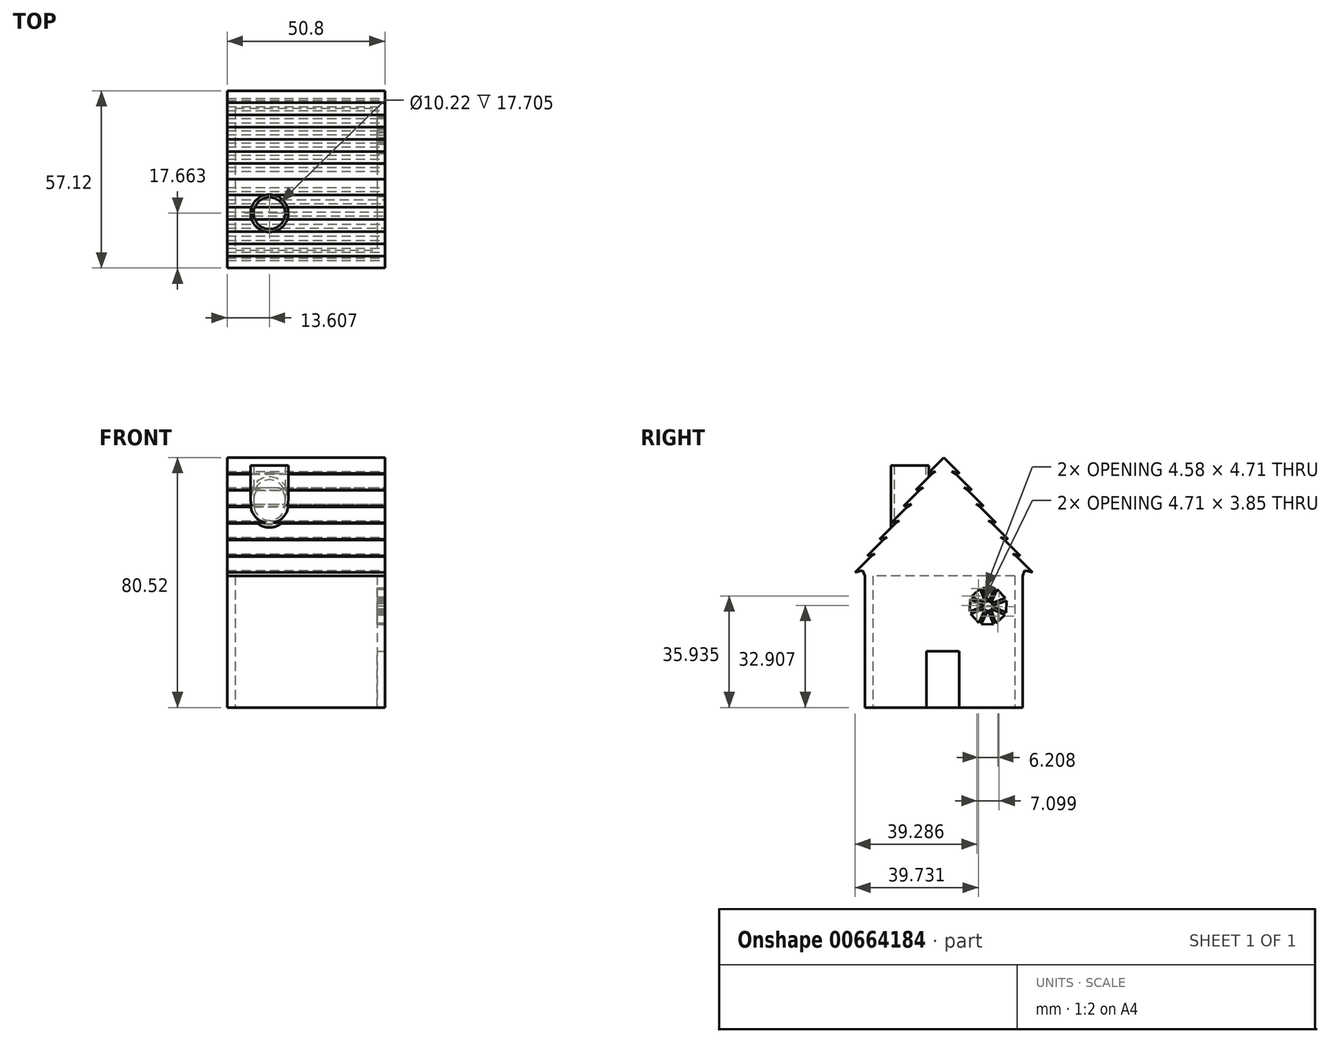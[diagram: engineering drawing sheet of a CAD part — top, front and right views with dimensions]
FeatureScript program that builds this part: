
annotation { "Feature Type Name" : "Feature", "Feature Type Description" : "" }
export const myFeature = defineFeature(function(context is Context, id is Id, definition is map)
    precondition{}
    {
        {
            var Q0;
            Q0=qCreatedBy(makeId("Top.planeOp"),FACE);
            var sketch = newSketch(context, id + "F0", { "sketchPlane" : qUnion([Q0])});
            skLineSegment(sketch, "E0.bottom", {"start": v(-25.4, 25.4) * mm, "end": v(25.4, 25.4) * mm});
            skLineSegment(sketch, "E0.top", {"start": v(-25.4, -25.4) * mm, "end": v(25.4, -25.4) * mm});
            skLineSegment(sketch, "E0.left", {"start": v(-25.4, 25.4) * mm, "end": v(-25.4, -25.4) * mm});
            skLineSegment(sketch, "E0.right", {"start": v(25.4, 25.4) * mm, "end": v(25.4, -25.4) * mm});
            skLineSegment(sketch, "E1.bottom", {"start": v(-22.86, 22.86) * mm, "end": v(22.86, 22.86) * mm});
            skLineSegment(sketch, "E1.top", {"start": v(-22.86, -22.86) * mm, "end": v(22.86, -22.86) * mm});
            skLineSegment(sketch, "E1.left", {"start": v(-22.86, 22.86) * mm, "end": v(-22.86, -22.86) * mm});
            skLineSegment(sketch, "E1.right", {"start": v(22.86, 22.86) * mm, "end": v(22.86, -22.86) * mm});
            skPoint(sketch, "E2", {"position": v(0, 22.86) * mm});
            skPoint(sketch, "E3", {"position": v(22.86, 0) * mm});
            skSolve(sketch);
        }
        {
            var Q0;
            Q0 = qSketchRegion(id + "F0", true);
            extrude(context, id + "F1", {"entities" : qUnion([Q0]), "depth" : 42.42 * mm, "offsetDistance" : 25.4 * mm});
        }
        {
            var Q0;
            Q0=makeQuery(id+"F1.opExtrude","SWEPT_FACE",FACE,{"disambiguationData":[OSD([sQuery(id+"F0.wireOp",EDGE,"E0.right")])]});
            var sketch = newSketch(context, id + "F2", { "sketchPlane" : qUnion([Q0])});
            skLineSegment(sketch, "E4.bottom", {"start": v(4.93, 0) * mm, "end": v(-5.52, 0) * mm});
            skLineSegment(sketch, "E4.top", {"start": v(4.93, 18.06) * mm, "end": v(-5.52, 18.06) * mm});
            skLineSegment(sketch, "E4.left", {"start": v(4.93, 0) * mm, "end": v(4.93, 18.06) * mm});
            skLineSegment(sketch, "E4.right", {"start": v(-5.52, 0) * mm, "end": v(-5.52, 18.06) * mm});
            skSolve(sketch);
        }
        {
            var Q0;
            Q0 = qSketchRegion(id + "F2", true);
            extrude(context, id + "F3", {"entities" : qUnion([Q0]), "operationType" : NewBodyOperationType.REMOVE, "oppositeDirection" : true, "depth" : 33.02 * mm, "offsetDistance" : 25.4 * mm});
        }
        {
            var Q0;
            Q0=makeQuery(id+"F1.opExtrude","SWEPT_FACE",FACE,{"disambiguationData":[OSD([sQuery(id+"F0.wireOp",EDGE,"E0.right")])]});
            var sketch = newSketch(context, id + "F4", { "sketchPlane" : qUnion([Q0])});
            skLineSegment(sketch, "E5", {"start": v(25.4, 42.42) * mm, "end": v(0, 80.52) * mm, "construction": true});
            skLineSegment(sketch, "E6", {"start": v(0, 80.52) * mm, "end": v(-25.4, 42.42) * mm, "construction": true});
            skLineSegment(sketch, "E7", {"start": v(0, 80.52) * mm, "end": v(5.08, 75.44) * mm});
            skLineSegment(sketch, "E8", {"start": v(5.08, 75.44) * mm, "end": v(2.63, 76.1) * mm});
            skLineSegment(sketch, "E9.0.1.0", {"start": v(3.91, 75.2) * mm, "end": v(9, 70.12) * mm});
            skLineSegment(sketch, "E9.0.1.1", {"start": v(9, 70.12) * mm, "end": v(6.54, 70.78) * mm});
            skLineSegment(sketch, "E9.0.2.0", {"start": v(7.83, 69.88) * mm, "end": v(12.9, 64.8) * mm});
            skLineSegment(sketch, "E9.0.2.1", {"start": v(12.9, 64.8) * mm, "end": v(10.45, 65.46) * mm});
            skLineSegment(sketch, "E9.0.3.0", {"start": v(11.74, 64.56) * mm, "end": v(16.82, 59.48) * mm});
            skLineSegment(sketch, "E9.0.3.1", {"start": v(16.82, 59.48) * mm, "end": v(14.36, 60.14) * mm});
            skLineSegment(sketch, "E9.0.4.0", {"start": v(15.65, 59.24) * mm, "end": v(20.73, 54.16) * mm});
            skLineSegment(sketch, "E9.0.4.1", {"start": v(20.73, 54.16) * mm, "end": v(18.28, 54.82) * mm});
            skLineSegment(sketch, "E9.0.5.0", {"start": v(19.56, 53.92) * mm, "end": v(24.64, 48.84) * mm});
            skLineSegment(sketch, "E9.0.5.1", {"start": v(24.64, 48.84) * mm, "end": v(22.2, 49.5) * mm});
            skLineSegment(sketch, "E9.0.6.0", {"start": v(23.48, 48.6) * mm, "end": v(28.56, 43.52) * mm});
            skLineSegment(sketch, "E9.0.6.1", {"start": v(28.56, 43.52) * mm, "end": v(26.1, 44.17) * mm});
            skLineSegment(sketch, "E9.direction1", {"start": v(2.63, 76.1) * mm, "end": v(28.03, 76.1) * mm, "construction": true});
            skLineSegment(sketch, "E9.direction2", {"start": v(2.63, 76.1) * mm, "end": v(6.54, 70.78) * mm, "construction": true});
            skLineSegment(sketch, "E10", {"start": v(2.63, 76.1) * mm, "end": v(3.91, 75.2) * mm});
            skLineSegment(sketch, "E11", {"start": v(6.54, 70.78) * mm, "end": v(7.83, 69.88) * mm});
            skLineSegment(sketch, "E12", {"start": v(10.45, 65.46) * mm, "end": v(11.74, 64.56) * mm});
            skLineSegment(sketch, "E13", {"start": v(14.36, 60.14) * mm, "end": v(15.65, 59.24) * mm});
            skLineSegment(sketch, "E14", {"start": v(18.28, 54.82) * mm, "end": v(19.56, 53.92) * mm});
            skLineSegment(sketch, "E15", {"start": v(22.2, 49.5) * mm, "end": v(23.48, 48.6) * mm});
            skLineSegment(sketch, "E16", {"start": v(26.1, 44.17) * mm, "end": v(25.4, 42.42) * mm});
            skLineSegment(sketch, "E17", {"start": v(0, 80.52) * mm, "end": v(0, 42.42) * mm, "construction": true});
            skLineSegment(sketch, "E18.MirrorCS", {"start": v(-26.1, 44.17) * mm, "end": v(-25.4, 42.42) * mm});
            skLineSegment(sketch, "E19.MirrorCS", {"start": v(-28.56, 43.52) * mm, "end": v(-26.1, 44.17) * mm});
            skLineSegment(sketch, "E20.MirrorCS", {"start": v(-23.48, 48.6) * mm, "end": v(-28.56, 43.52) * mm});
            skLineSegment(sketch, "E21.MirrorCS", {"start": v(-22.2, 49.5) * mm, "end": v(-23.48, 48.6) * mm});
            skLineSegment(sketch, "E22.MirrorCS", {"start": v(-24.64, 48.84) * mm, "end": v(-22.2, 49.5) * mm});
            skLineSegment(sketch, "E23.MirrorCS", {"start": v(-19.56, 53.92) * mm, "end": v(-24.64, 48.84) * mm});
            skLineSegment(sketch, "E24.MirrorCS", {"start": v(-18.28, 54.82) * mm, "end": v(-19.56, 53.92) * mm});
            skLineSegment(sketch, "E25.MirrorCS", {"start": v(-20.73, 54.16) * mm, "end": v(-18.28, 54.82) * mm});
            skLineSegment(sketch, "E26.MirrorCS", {"start": v(-15.65, 59.24) * mm, "end": v(-20.73, 54.16) * mm});
            skLineSegment(sketch, "E27.MirrorCS", {"start": v(-14.36, 60.14) * mm, "end": v(-15.65, 59.24) * mm});
            skLineSegment(sketch, "E28.MirrorCS", {"start": v(-16.82, 59.48) * mm, "end": v(-14.36, 60.14) * mm});
            skLineSegment(sketch, "E29.MirrorCS", {"start": v(-11.74, 64.56) * mm, "end": v(-16.82, 59.48) * mm});
            skLineSegment(sketch, "E30.MirrorCS", {"start": v(-10.45, 65.46) * mm, "end": v(-11.74, 64.56) * mm});
            skLineSegment(sketch, "E31.MirrorCS", {"start": v(-12.9, 64.8) * mm, "end": v(-10.45, 65.46) * mm});
            skLineSegment(sketch, "E32.MirrorCS", {"start": v(-7.83, 69.88) * mm, "end": v(-12.9, 64.8) * mm});
            skLineSegment(sketch, "E33.MirrorCS", {"start": v(-6.54, 70.78) * mm, "end": v(-7.83, 69.88) * mm});
            skLineSegment(sketch, "E34.MirrorCS", {"start": v(-9, 70.12) * mm, "end": v(-6.54, 70.78) * mm});
            skLineSegment(sketch, "E35.MirrorCS", {"start": v(-3.91, 75.2) * mm, "end": v(-9, 70.12) * mm});
            skLineSegment(sketch, "E36.MirrorCS", {"start": v(-2.63, 76.1) * mm, "end": v(-3.91, 75.2) * mm});
            skLineSegment(sketch, "E37.MirrorCS", {"start": v(-5.08, 75.44) * mm, "end": v(-2.63, 76.1) * mm});
            skLineSegment(sketch, "E38.MirrorCS", {"start": v(0, 80.52) * mm, "end": v(-5.08, 75.44) * mm});
            skLineSegment(sketch, "E39", {"start": v(-25.4, 42.42) * mm, "end": v(25.4, 42.42) * mm});
            skSolve(sketch);
        }
        {
            var Q0;
            Q0 = qSketchRegion(id + "F4", true);
            extrude(context, id + "F5", {"entities" : qUnion([Q0]), "operationType" : NewBodyOperationType.ADD, "oppositeDirection" : true, "depth" : 50.8 * mm, "offsetDistance" : 25.4 * mm});
        }
        {
            var Q0;
            Q0=makeQuery(id+"F5.opExtrude","SWEPT_FACE",FACE,{"disambiguationData":[OSD([sQuery(id+"F4.wireOp",EDGE,"E39")])]});
            var sketch = newSketch(context, id + "F6", { "sketchPlane" : qUnion([Q0])});
            skCircle(sketch, "E40", {"center": v(-11.8, 10.9) * mm, "radius": 6.05 * mm});
            skCircle(sketch, "E41", {"center": v(-11.8, 10.9) * mm, "radius": 5.11 * mm});
            skSolve(sketch);
        }
        {
            var Q0;
            Q0 = qSketchRegion(id + "F6", true);
            extrude(context, id + "F7", {"entities" : qUnion([Q0]), "operationType" : NewBodyOperationType.ADD, "oppositeDirection" : true, "depth" : 35.56 * mm, "offsetDistance" : 25.4 * mm});
        }
        {
            var Q0;
            Q0=makeQuery(id+"F5.boolean.opBoolean","MERGE",FACE,{"derivedFrom":[makeQuery(id+"F1.opExtrude","SWEPT_FACE",FACE,{"disambiguationData":[OSD([sQuery(id+"F0.wireOp",EDGE,"E0.right")])]}),makeQuery(id+"F5.opExtrude","CAP_FACE",FACE,{"disambiguationData":[OSD([sQuery(id+"F4.wireOp",EDGE,"E7"),sQuery(id+"F4.wireOp",EDGE,"E8"),sQuery(id+"F4.wireOp",EDGE,"E9.0.1.0"),sQuery(id+"F4.wireOp",EDGE,"E9.0.1.1"),sQuery(id+"F4.wireOp",EDGE,"E9.0.2.0"),sQuery(id+"F4.wireOp",EDGE,"E9.0.2.1"),sQuery(id+"F4.wireOp",EDGE,"E9.0.3.0"),sQuery(id+"F4.wireOp",EDGE,"E9.0.3.1"),sQuery(id+"F4.wireOp",EDGE,"E9.0.4.0"),sQuery(id+"F4.wireOp",EDGE,"E9.0.4.1"),sQuery(id+"F4.wireOp",EDGE,"E9.0.5.0"),sQuery(id+"F4.wireOp",EDGE,"E9.0.5.1"),sQuery(id+"F4.wireOp",EDGE,"E9.0.6.0"),sQuery(id+"F4.wireOp",EDGE,"E9.0.6.1"),sQuery(id+"F4.wireOp",EDGE,"E10"),sQuery(id+"F4.wireOp",EDGE,"E11"),sQuery(id+"F4.wireOp",EDGE,"E12"),sQuery(id+"F4.wireOp",EDGE,"E13"),sQuery(id+"F4.wireOp",EDGE,"E14"),sQuery(id+"F4.wireOp",EDGE,"E15"),sQuery(id+"F4.wireOp",EDGE,"E16"),sQuery(id+"F4.wireOp",EDGE,"E18.MirrorCS"),sQuery(id+"F4.wireOp",EDGE,"E19.MirrorCS"),sQuery(id+"F4.wireOp",EDGE,"E20.MirrorCS"),sQuery(id+"F4.wireOp",EDGE,"E21.MirrorCS"),sQuery(id+"F4.wireOp",EDGE,"E22.MirrorCS"),sQuery(id+"F4.wireOp",EDGE,"E23.MirrorCS"),sQuery(id+"F4.wireOp",EDGE,"E24.MirrorCS"),sQuery(id+"F4.wireOp",EDGE,"E25.MirrorCS"),sQuery(id+"F4.wireOp",EDGE,"E26.MirrorCS"),sQuery(id+"F4.wireOp",EDGE,"E27.MirrorCS"),sQuery(id+"F4.wireOp",EDGE,"E28.MirrorCS"),sQuery(id+"F4.wireOp",EDGE,"E29.MirrorCS"),sQuery(id+"F4.wireOp",EDGE,"E30.MirrorCS"),sQuery(id+"F4.wireOp",EDGE,"E31.MirrorCS"),sQuery(id+"F4.wireOp",EDGE,"E32.MirrorCS"),sQuery(id+"F4.wireOp",EDGE,"E33.MirrorCS"),sQuery(id+"F4.wireOp",EDGE,"E34.MirrorCS"),sQuery(id+"F4.wireOp",EDGE,"E35.MirrorCS"),sQuery(id+"F4.wireOp",EDGE,"E36.MirrorCS"),sQuery(id+"F4.wireOp",EDGE,"E37.MirrorCS"),sQuery(id+"F4.wireOp",EDGE,"E38.MirrorCS"),sQuery(id+"F4.wireOp",EDGE,"E39")])],"isStart":true})]});
            var sketch = newSketch(context, id + "F8", { "sketchPlane" : qUnion([Q0])});
            skCircle(sketch, "E42.cCircle", {"center": v(14.28, 32.7) * mm, "radius": 6.3 * mm, "construction": true});
            skLineSegment(sketch, "E42.0", {"start": v(8.07, 35.53) * mm, "end": v(11.89, 39.1) * mm, "construction": true});
            skLineSegment(sketch, "E42.1", {"start": v(11.89, 39.1) * mm, "end": v(17.1, 38.91) * mm, "construction": true});
            skLineSegment(sketch, "E42.2", {"start": v(17.1, 38.91) * mm, "end": v(20.66, 35.1) * mm, "construction": true});
            skLineSegment(sketch, "E42.3", {"start": v(20.66, 35.1) * mm, "end": v(20.48, 29.88) * mm, "construction": true});
            skLineSegment(sketch, "E42.4", {"start": v(20.48, 29.88) * mm, "end": v(16.67, 26.32) * mm, "construction": true});
            skLineSegment(sketch, "E42.5", {"start": v(16.67, 26.32) * mm, "end": v(11.45, 26.5) * mm, "construction": true});
            skLineSegment(sketch, "E42.6", {"start": v(11.45, 26.5) * mm, "end": v(7.9, 30.32) * mm, "construction": true});
            skLineSegment(sketch, "E42.7", {"start": v(7.9, 30.32) * mm, "end": v(8.07, 35.53) * mm, "construction": true});
            skPoint(sketch, "E42.0.midPoint", {"position": v(9.98, 37.31) * mm});
            skLineSegment(sketch, "E43", {"start": v(11.89, 39.1) * mm, "end": v(14.28, 32.7) * mm, "construction": true});
            skLineSegment(sketch, "E44", {"start": v(17.1, 38.91) * mm, "end": v(14.28, 32.7) * mm, "construction": true});
            skLineSegment(sketch, "E45.6", {"start": v(19.05, 43.64) * mm, "end": v(19.14, 43.88) * mm});
            skLineSegment(sketch, "E45.9", {"start": v(-19.14, 43.88) * mm, "end": v(-19.05, 43.64) * mm});
            skLineSegment(sketch, "E46.0", {"start": v(16.4, 38.48) * mm, "end": v(14.32, 33.9) * mm});
            skLineSegment(sketch, "E46.1", {"start": v(12.55, 38.61) * mm, "end": v(16.4, 38.48) * mm});
            skLineSegment(sketch, "E46.2", {"start": v(12.55, 38.61) * mm, "end": v(14.32, 33.9) * mm});
            skLineSegment(sketch, "E47.1.0", {"start": v(11.7, 38.3) * mm, "end": v(13.46, 33.58) * mm});
            skLineSegment(sketch, "E47.1.1", {"start": v(8.88, 35.66) * mm, "end": v(13.46, 33.58) * mm});
            skLineSegment(sketch, "E47.1.2", {"start": v(8.88, 35.66) * mm, "end": v(11.7, 38.3) * mm});
            skLineSegment(sketch, "E47.2.0", {"start": v(8.5, 34.83) * mm, "end": v(13.08, 32.75) * mm});
            skLineSegment(sketch, "E47.2.1", {"start": v(8.37, 30.98) * mm, "end": v(13.08, 32.75) * mm});
            skLineSegment(sketch, "E47.2.2", {"start": v(8.37, 30.98) * mm, "end": v(8.5, 34.83) * mm});
            skLineSegment(sketch, "E47.3.0", {"start": v(8.7, 30.13) * mm, "end": v(13.4, 31.9) * mm});
            skLineSegment(sketch, "E47.3.1", {"start": v(11.32, 27.31) * mm, "end": v(13.4, 31.9) * mm});
            skLineSegment(sketch, "E47.3.2", {"start": v(11.32, 27.31) * mm, "end": v(8.7, 30.13) * mm});
            skLineSegment(sketch, "E47.4.0", {"start": v(12.15, 26.93) * mm, "end": v(14.23, 31.51) * mm});
            skLineSegment(sketch, "E47.4.1", {"start": v(16, 26.8) * mm, "end": v(14.23, 31.51) * mm});
            skLineSegment(sketch, "E47.4.2", {"start": v(16, 26.8) * mm, "end": v(12.15, 26.93) * mm});
            skLineSegment(sketch, "E47.5.0", {"start": v(16.85, 27.12) * mm, "end": v(15.1, 31.83) * mm});
            skLineSegment(sketch, "E47.5.1", {"start": v(19.67, 29.75) * mm, "end": v(15.1, 31.83) * mm});
            skLineSegment(sketch, "E47.5.2", {"start": v(19.67, 29.75) * mm, "end": v(16.85, 27.12) * mm});
            skLineSegment(sketch, "E47.6.0", {"start": v(20.05, 30.58) * mm, "end": v(15.47, 32.66) * mm});
            skLineSegment(sketch, "E47.6.1", {"start": v(20.18, 34.43) * mm, "end": v(15.47, 32.66) * mm});
            skLineSegment(sketch, "E47.6.2", {"start": v(20.18, 34.43) * mm, "end": v(20.05, 30.58) * mm});
            skLineSegment(sketch, "E47.7.0", {"start": v(19.86, 35.28) * mm, "end": v(15.15, 33.52) * mm});
            skLineSegment(sketch, "E47.7.1", {"start": v(17.23, 38.1) * mm, "end": v(15.15, 33.52) * mm});
            skLineSegment(sketch, "E47.7.2", {"start": v(17.23, 38.1) * mm, "end": v(19.86, 35.28) * mm});
            skSolve(sketch);
        }
        {
            var Q0;
            Q0=makeQuery(id+"F8.imprint","IMPRINT",FACE,{"disambiguationData":[TD([[makeQuery(id+"F8.imprint","IMPRINT",EDGE,{"derivedFrom":sQuery(id+"F8.wireOp",EDGE,"E47.1.0")}),-1.0]])]});
            var Q1;
            Q1=makeQuery(id+"F8.imprint","IMPRINT",FACE,{"disambiguationData":[TD([[makeQuery(id+"F8.imprint","IMPRINT",EDGE,{"derivedFrom":sQuery(id+"F8.wireOp",EDGE,"E46.0")}),-1.0]])]});
            var Q2;
            Q2=makeQuery(id+"F8.imprint","IMPRINT",FACE,{"disambiguationData":[TD([[makeQuery(id+"F8.imprint","IMPRINT",EDGE,{"derivedFrom":sQuery(id+"F8.wireOp",EDGE,"E47.7.0")}),-1.0]])]});
            var Q3;
            Q3=makeQuery(id+"F8.imprint","IMPRINT",FACE,{"disambiguationData":[TD([[makeQuery(id+"F8.imprint","IMPRINT",EDGE,{"derivedFrom":sQuery(id+"F8.wireOp",EDGE,"E47.2.0")}),-1.0]])]});
            var Q4;
            Q4=makeQuery(id+"F8.imprint","IMPRINT",FACE,{"disambiguationData":[TD([[makeQuery(id+"F8.imprint","IMPRINT",EDGE,{"derivedFrom":sQuery(id+"F8.wireOp",EDGE,"E47.3.0")}),-1.0]])]});
            var Q5;
            Q5=makeQuery(id+"F8.imprint","IMPRINT",FACE,{"disambiguationData":[TD([[makeQuery(id+"F8.imprint","IMPRINT",EDGE,{"derivedFrom":sQuery(id+"F8.wireOp",EDGE,"E47.4.0")}),-1.0]])]});
            var Q6;
            Q6=makeQuery(id+"F8.imprint","IMPRINT",FACE,{"disambiguationData":[TD([[makeQuery(id+"F8.imprint","IMPRINT",EDGE,{"derivedFrom":sQuery(id+"F8.wireOp",EDGE,"E47.5.0")}),-1.0]])]});
            var Q7;
            Q7=makeQuery(id+"F8.imprint","IMPRINT",FACE,{"disambiguationData":[TD([[makeQuery(id+"F8.imprint","IMPRINT",EDGE,{"derivedFrom":sQuery(id+"F8.wireOp",EDGE,"E47.6.0")}),-1.0]])]});
            extrude(context, id + "F9", {"entities" : qUnion([Q0, Q1, Q2, Q3, Q4, Q5, Q6, Q7]), "operationType" : NewBodyOperationType.REMOVE, "oppositeDirection" : true, "depth" : 25.4 * mm, "offsetDistance" : 25.4 * mm});
        }
    });
